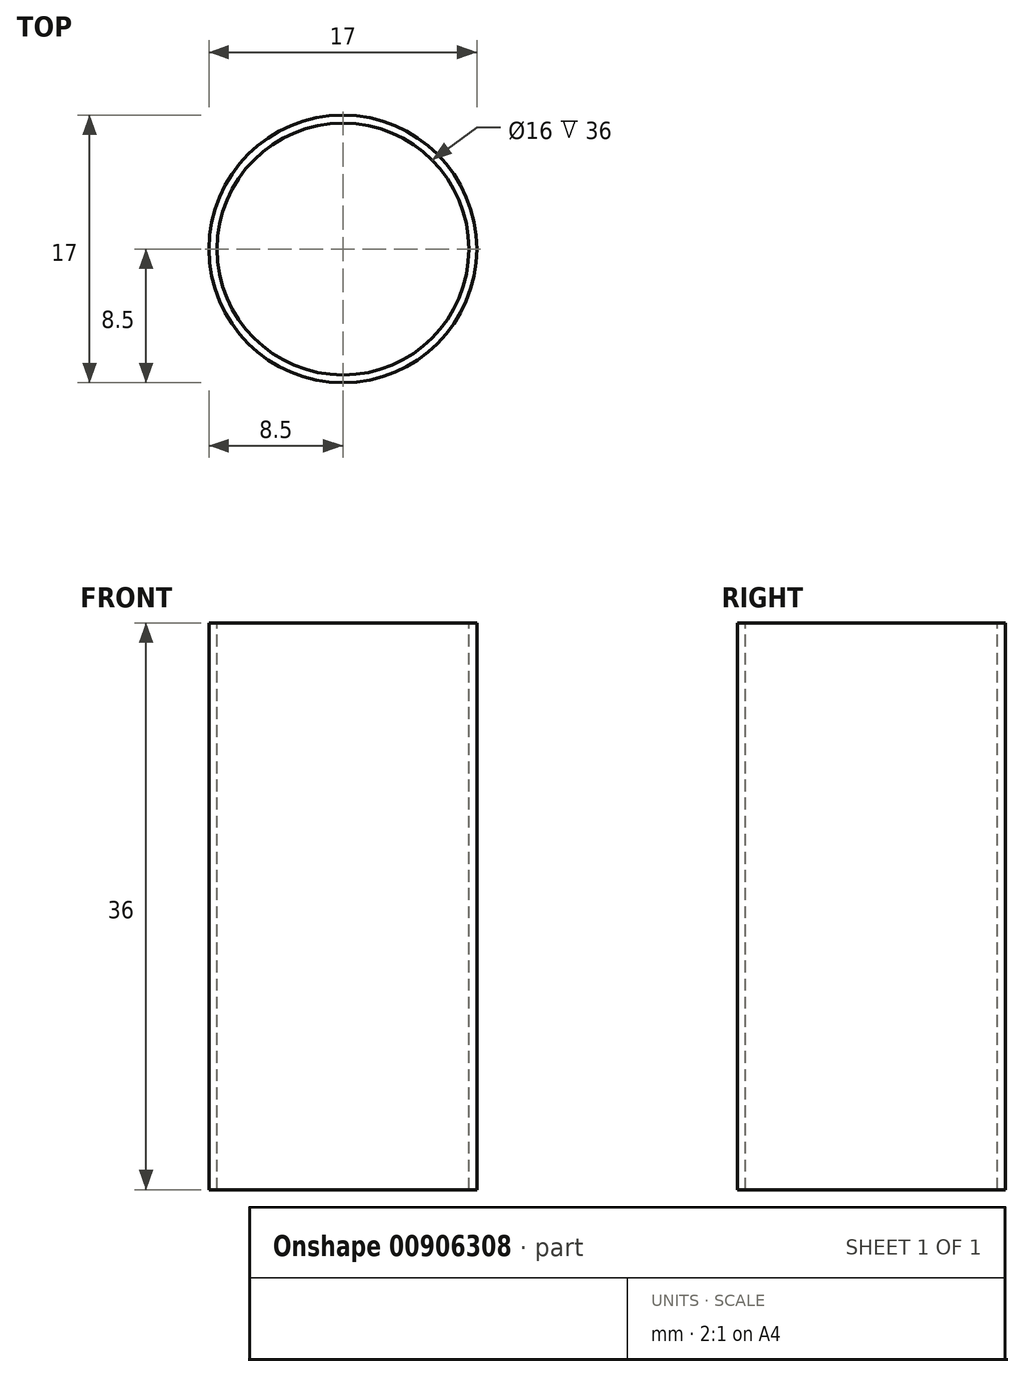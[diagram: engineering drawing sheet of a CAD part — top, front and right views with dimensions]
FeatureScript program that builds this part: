
annotation { "Feature Type Name" : "Feature", "Feature Type Description" : "" }
export const myFeature = defineFeature(function(context is Context, id is Id, definition is map)
    precondition{}
    {
        {
            var Q0;
            Q0=qCreatedBy(makeId("Top.planeOp"),FACE);
            var sketch = newSketch(context, id + "F0", { "sketchPlane" : qUnion([Q0])});
            skCircle(sketch, "E0", {"center": v(0, 0) * mm, "radius": 8.5 * mm});
            skCircle(sketch, "E1", {"center": v(0, 0) * mm, "radius": 8 * mm});
            skSolve(sketch);
        }
        {
            var Q0;
            Q0=qCreatedBy(makeId("Front.planeOp"),FACE);
            var sketch = newSketch(context, id + "F1", { "sketchPlane" : qUnion([Q0])});
            skLineSegment(sketch, "E2", {"start": v(0, 0) * mm, "end": v(0, 36) * mm});
            skSolve(sketch);
        }
        {
            var Q0;
            Q0=makeQuery(id+"F0.imprint","IMPRINT",FACE,{"disambiguationData":[TD([[makeQuery(id+"F0.imprint","IMPRINT",EDGE,{"derivedFrom":sQuery(id+"F0.wireOp",EDGE,"E0")}),1.0]])]});
            var Q1;
            Q1=sQuery(id+"F1.wireOp",EDGE,"E2");
            sweep(context, id + "F2", {"profiles" : qUnion([Q0]), "path" : qUnion([Q1])});
        }
    });
